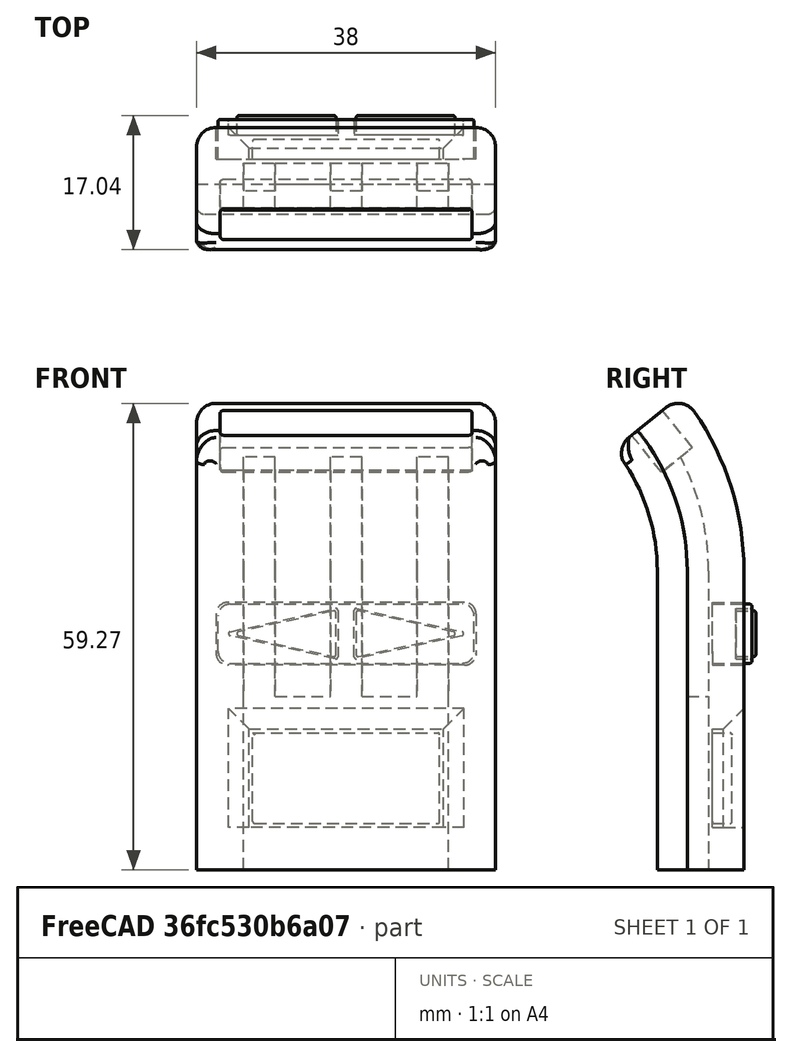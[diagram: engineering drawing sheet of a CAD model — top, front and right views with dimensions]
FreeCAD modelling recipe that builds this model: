
FCSTD DOCUMENT  (FreeCAD 0.20R29603 (Git))
Label: arm
License: All rights reserved
LicenseURL: http://en.wikipedia.org/wiki/All_rights_reserved
objects: Part::Box×22, Part::MultiFuse×15, Part::Cut×13, Part::Fillet×10, Part::Cylinder×9, Sketcher::SketchObject×4, PartDesign::Pad×4, PartDesign::Body×4, Part::MultiCommon×3, Part::Wedge×2, Mesh::Feature×1, Spreadsheet::Sheet×1
note: 90 computed .brp shape members not serialized (recipe doc carries the construction recipe); baked Part::Feature solids carry a one-line shape summary decoded from their .brp

FEATURE [Mesh::Feature] Display_Arm
  Placement = pos=(0,13.65,-35) rot=(0,0,1;0rad)
FEATURE [Part::Cylinder] Cylinder  label="Underside cylinder"
  Angle = 360
  AttacherType = Attacher::AttachEngine3D
  FirstAngle = 0
  Height = 42
  Placement = pos=(-2,-6.5,0) rot=(0,-1,0;4.71239rad)
  Radius = 24.5
  SecondAngle = 0
  expr: .Placement.Base.y = -Spreadsheet.B1 + 18
  expr: Radius = Spreadsheet.B1
FEATURE [Spreadsheet::Sheet] Spreadsheet
  cells = A1=underside radius; B1=24.5; D1=triangle width; E1=5.9; G1=6.5; A2=topside radius; B2=40; D2=triangle height; E2=12.5; F2=1.04; G2=13.75; A3=Arm thickness; B3=11; D3=triangle filet; E3=0.25; G3==E3 * F2; A4=bisect radius; B4=28.3; D4=filet top; E4=0.25; G4==E4 * F2; A5=led channel cut; B5=31
FEATURE [Part::Box] Box  label="Cube"
  AttacherType = Attacher::AttachEngine3D
  Height = 52
  Length = 42
  Placement = pos=(-2,18,0) rot=(1,0,0;3.14159rad)
  Width = 49
  expr: Width = Spreadsheet.B1 * 2
FEATURE [Part::Cylinder] Cylinder001  label="top cylinder"
  Angle = 360
  AttacherType = Attacher::AttachEngine3D
  FirstAngle = 0
  Height = 42
  Placement = pos=(-2,-6.5,0) rot=(0,1,0;1.5708rad)
  Radius = 35.5
  SecondAngle = 0
  expr: .Placement.Base.y = -Spreadsheet.B1 + 18
  expr: Radius = Spreadsheet.B1 + Spreadsheet.B3
FEATURE [Part::Box] Box001  label="Cube001"
  AttacherType = Attacher::AttachEngine3D
  Height = 52
  Length = 42
  Placement = pos=(-2,29,0) rot=(1,0,0;3.14159rad)
  Width = 71
  expr: .Placement.Base.y = 18 + Spreadsheet.B3
  expr: Width = (Spreadsheet.B1 + Spreadsheet.B3) * 2
FEATURE [Part::MultiFuse] Fusion  label="Underside cut"
  Shapes = -> [Cylinder,Box]
FEATURE [Part::MultiFuse] Fusion001  label="Topside intersect"
  Shapes = -> [Cylinder001,Box001]
FEATURE [Part::Box] Box002  label="Cube002"
  AttacherType = Attacher::AttachEngine3D
  Height = 76
  Length = 38
  Placement = pos=(0,10,-38) rot=(0,0,1;0rad)
  Width = 20
FEATURE [Part::Cut] Cut
  Base = -> Box002
  Tool = -> Fusion
FEATURE [Part::MultiCommon] Common
  Shapes = -> [Cut,Fusion001]
FEATURE [Part::Box] Box003  label="Cube003"
  AttacherType = Attacher::AttachEngine3D
  Height = 27
  Length = 56
  Placement = pos=(-5,-6.5,0) rot=(-1,0,0;5.60251rad)
  Width = 48
FEATURE [Part::Cut] Cut001
  Base = -> Common
  Tool = -> Box003
FEATURE [Part::Fillet] Fillet
  Base = -> Cut001
  Edges = 12 edges: [Edge1 r=2.5,Edge2 r=2.5,Edge3 r=2.5,Edge5 r=1,Edge6 r=1,Edge7 r=2.5,Edge8 r=2.5,Edge9 r=2.5,Edge10 r=2.5,Edge12 r=2.5,Edge17 r=1,Edge18 r=1]
FEATURE [Part::Box] Box004  label="Cube004"
  AttacherType = Attacher::AttachEngine3D
  Height = 52
  Length = 42
  Placement = pos=(-2,21.8,0) rot=(1,0,0;3.14159rad)
  Width = 56.6
  expr: .Placement.Base.y = 18 + Spreadsheet.B4 - Spreadsheet.B1
  expr: Width = Spreadsheet.B4 * 2
FEATURE [Part::Cylinder] Cylinder002  label="top cylinder001"
  Angle = 360
  AttacherType = Attacher::AttachEngine3D
  FirstAngle = 0
  Height = 42
  Placement = pos=(-2,-6.5,0) rot=(0,1,0;1.5708rad)
  Radius = 28.3
  SecondAngle = 0
  expr: .Placement.Base.y = -Spreadsheet.B1 + 18
  expr: Radius = Spreadsheet.B4
FEATURE [Part::MultiFuse] Fusion002  label="Bisect intersect"
  Shapes = -> [Box004,Cylinder002]
FEATURE [Sketcher::SketchObject] Sketch
  FullyConstrained = true
  MapMode = 5
  Placement = pos=(0,0,0) rot=(1,0,0;1.5708rad)
  Support = -> [XZ_Plane]
  expr: .Constraints.Base filet = Spreadsheet.E3
  expr: .Constraints.Base filet 2 = Spreadsheet.E3
  expr: .Constraints.base = Spreadsheet.E1
  expr: .Constraints.filet top = Spreadsheet.E4
  expr: Constraints[6] = (Spreadsheet.E1 * Spreadsheet.E1 + Spreadsheet.E2 * Spreadsheet.E2) ^ (1 / 2)
  expr: Constraints[7] = (Spreadsheet.E1 * Spreadsheet.E1 + Spreadsheet.E2 * Spreadsheet.E2) ^ (1 / 2)
  sketch-geometry (10):
    g0: LineSegment StartX=-0.24424 StartY=5.95617 StartZ=0 EndX=-2.88373 EndY=-6.12642 EndZ=0
    g1: LineSegment StartX=-2.63949 StartY=-6.42977 StartZ=0 EndX=2.63949 EndY=-6.42977 EndZ=0
    g2: LineSegment StartX=2.88373 StartY=-6.12642 StartZ=0 EndX=0.24424 EndY=5.95617 EndZ=0
    g3: Circle CenterX=0 CenterY=0 CenterZ=0 NormalX=0 NormalY=0 NormalZ=1 AngleXU=0 Radius=7.07421
    g4: ArcOfCircle CenterX=1.3e-15 CenterY=5.90282 CenterZ=0 NormalX=0 NormalY=0 NormalZ=1 AngleXU=0 Radius=0.25 StartAngle=0.215075 EndAngle=2.92652
    g5: GeomPoint X=1.5e-15 Y=7.07421 Z=0
    g6: ArcOfCircle CenterX=-2.63949 CenterY=-6.17977 CenterZ=0 NormalX=0 NormalY=0 NormalZ=1 AngleXU=0 Radius=0.25 StartAngle=2.92652 EndAngle=4.71239
    g7: GeomPoint X=-2.95 Y=-6.42977 Z=0
    g8: ArcOfCircle CenterX=2.63949 CenterY=-6.17977 CenterZ=0 NormalX=0 NormalY=0 NormalZ=1 AngleXU=0 Radius=0.25 StartAngle=4.71239 EndAngle=6.49826
    g9: GeomPoint X=2.95 Y=-6.42977 Z=0
  constraints (23):
    c: PointOnObject(g7,g3)
    c: PointOnObject(g9,g3)
    c: PointOnObject(g5,g3)
    c: Coincident(g3,g-1)
    c: Horizontal(g1)
    c: Distance(g9,g7) = 5.9  'base'
    c: Distance(g9,g5) = 13.8224
    c: Distance(g7,g5) = 13.8224
    c: PointOnObject(g5,g0)
    c: PointOnObject(g5,g2)
    c: Tangent(g0,g4) = -1.5708
    c: Tangent(g2,g4) = -1.5708
    c: Radius(g4) = 0.25  'filet top'
    c: PointOnObject(g7,g0)
    c: PointOnObject(g7,g1)
    c: Tangent(g0,g6) = -1.5708
    c: Tangent(g1,g6) = -1.5708
    c: PointOnObject(g9,g1)
    c: PointOnObject(g9,g2)
    c: Tangent(g1,g8) = -1.5708
    c: Tangent(g2,g8) = -1.5708
    c: Radius(g8) = 0.25  'Base filet'
    c: Radius(g6) = 0.25  'Base filet 2'
FEATURE [PartDesign::Pad] Pad
  Direction = (0,-1,2e-16)
  Length = 2.5
  Length2 = 10
  Placement = pos=(0,0,0) rot=(1,0,0;1.5708rad)
  Profile = -> Sketch
  ReferenceAxis = -> Sketch [N_Axis]
  Type = 0
FEATURE [PartDesign::Body] Body
  Group = -> [Sketch,Pad]
  Origin = -> Origin
  Placement = pos=(26.7,63,-8) rot=(0,1,0;1.5708rad)
  Tip = -> Pad
FEATURE [Sketcher::SketchObject] Sketch001
  FullyConstrained = true
  MapMode = 5
  Placement = pos=(0,0,0) rot=(1,0,0;1.5708rad)
  Support = -> [XZ_Plane]
  expr: .Constraints.Base filet = Spreadsheet.G3
  expr: .Constraints.Base filet 2 = Spreadsheet.G3
  expr: .Constraints.base = Spreadsheet.G1
  expr: .Constraints.filet top = Spreadsheet.G4
  expr: .Constraints.hyp 1 = (Spreadsheet.G1 ^ 2 + Spreadsheet.G2 ^ 2) ^ (1 / 2)
  expr: .Constraints.hyp 2 = (Spreadsheet.G1 ^ 2 + Spreadsheet.G2 ^ 2) ^ (1 / 2)
  sketch-geometry (10):
    g0: LineSegment StartX=-0.253994 StartY=6.62313 StartZ=0 EndX=-3.18097 EndY=-6.75781 EndZ=0
    g1: LineSegment StartX=-2.92698 StartY=-7.07337 StartZ=0 EndX=2.92698 EndY=-7.07337 EndZ=0
    g2: LineSegment StartX=3.18097 StartY=-6.75781 StartZ=0 EndX=0.253994 EndY=6.62313 EndZ=0
    g3: Circle CenterX=0 CenterY=0 CenterZ=0 NormalX=0 NormalY=0 NormalZ=1 AngleXU=0 Radius=7.78429
    g4: ArcOfCircle CenterX=-1e-15 CenterY=6.56757 CenterZ=0 NormalX=0 NormalY=0 NormalZ=1 AngleXU=0 Radius=0.26 StartAngle=0.21535 EndAngle=2.92624
    g5: GeomPoint X=-1.1e-15 Y=7.78429 Z=0
    g6: ArcOfCircle CenterX=-2.92698 CenterY=-6.81337 CenterZ=0 NormalX=0 NormalY=0 NormalZ=1 AngleXU=0 Radius=0.26 StartAngle=2.92624 EndAngle=4.71239
    g7: GeomPoint X=-3.25 Y=-7.07337 Z=0
    g8: ArcOfCircle CenterX=2.92698 CenterY=-6.81337 CenterZ=0 NormalX=0 NormalY=0 NormalZ=1 AngleXU=0 Radius=0.26 StartAngle=4.71239 EndAngle=6.49854
    g9: GeomPoint X=3.25 Y=-7.07337 Z=0
  constraints (23):
    c: PointOnObject(g7,g3)
    c: PointOnObject(g9,g3)
    c: PointOnObject(g5,g3)
    c: Coincident(g3,g-1)
    c: Horizontal(g1)
    c: Distance(g9,g7) = 6.5  'base'
    c: Distance(g9,g5) = 15.209  'hyp 1'
    c: Distance(g7,g5) = 15.209  'hyp 2'
    c: PointOnObject(g5,g0)
    c: PointOnObject(g5,g2)
    c: Tangent(g0,g4) = -1.5708
    c: Tangent(g2,g4) = -1.5708
    c: Radius(g4) = 0.26  'filet top'
    c: PointOnObject(g7,g0)
    c: PointOnObject(g7,g1)
    c: Tangent(g0,g6) = -1.5708
    c: Tangent(g1,g6) = -1.5708
    c: PointOnObject(g9,g1)
    c: PointOnObject(g9,g2)
    c: Tangent(g1,g8) = -1.5708
    c: Tangent(g2,g8) = -1.5708
    c: Radius(g8) = 0.26  'Base filet'
    c: Radius(g6) = 0.26  'Base filet 2'
FEATURE [PartDesign::Pad] Pad001
  Direction = (0,-1,2e-16)
  Length = 10
  Length2 = 10
  Placement = pos=(0,0,0) rot=(1,0,0;1.5708rad)
  Profile = -> Sketch001
  ReferenceAxis = -> Sketch001 [N_Axis]
  Type = 0
FEATURE [PartDesign::Body] Body001
  Group = -> [Sketch001,Pad001]
  Origin = -> Origin001
  Placement = pos=(27.1,63,-8) rot=(0,1,0;1.5708rad)
  Tip = -> Pad001
FEATURE [Sketcher::SketchObject] Sketch002
  FullyConstrained = true
  MapMode = 5
  Placement = pos=(0,0,0) rot=(1,0,0;1.5708rad)
  Support = -> [XZ_Plane]
  sketch-geometry (10):
    g0: LineSegment StartX=-0.24424 StartY=5.95617 StartZ=0 EndX=-2.88373 EndY=-6.12642 EndZ=0
    g1: LineSegment StartX=-2.63949 StartY=-6.42977 StartZ=0 EndX=2.63949 EndY=-6.42977 EndZ=0
    g2: LineSegment StartX=2.88373 StartY=-6.12642 StartZ=0 EndX=0.24424 EndY=5.95617 EndZ=0
    g3: Circle CenterX=0 CenterY=0 CenterZ=0 NormalX=0 NormalY=0 NormalZ=1 AngleXU=0 Radius=7.07421
    g4: ArcOfCircle CenterX=1.3e-15 CenterY=5.90282 CenterZ=0 NormalX=0 NormalY=0 NormalZ=1 AngleXU=0 Radius=0.25 StartAngle=0.215075 EndAngle=2.92652
    g5: GeomPoint X=1.5e-15 Y=7.07421 Z=0
    g6: ArcOfCircle CenterX=-2.63949 CenterY=-6.17977 CenterZ=0 NormalX=0 NormalY=0 NormalZ=1 AngleXU=0 Radius=0.25 StartAngle=2.92652 EndAngle=4.71239
    g7: GeomPoint X=-2.95 Y=-6.42977 Z=0
    g8: ArcOfCircle CenterX=2.63949 CenterY=-6.17977 CenterZ=0 NormalX=0 NormalY=0 NormalZ=1 AngleXU=0 Radius=0.25 StartAngle=4.71239 EndAngle=6.49826
    g9: GeomPoint X=2.95 Y=-6.42977 Z=0
  constraints (23):
    c: PointOnObject(g7,g3)
    c: PointOnObject(g9,g3)
    c: PointOnObject(g5,g3)
    c: Coincident(g3,g-1)
    c: Horizontal(g1)
    c: Distance(g9,g7) = 5.9  'base'
    c: Distance(g9,g5) = 13.8224
    c: Distance(g7,g5) = 13.8224
    c: PointOnObject(g5,g0)
    c: PointOnObject(g5,g2)
    c: Tangent(g0,g4) = -1.5708
    c: Tangent(g2,g4) = -1.5708
    c: Radius(g4) = 0.25  'filet top'
    c: PointOnObject(g7,g0)
    c: PointOnObject(g7,g1)
    c: Tangent(g0,g6) = -1.5708
    c: Tangent(g1,g6) = -1.5708
    c: PointOnObject(g9,g1)
    c: PointOnObject(g9,g2)
    c: Tangent(g1,g8) = -1.5708
    c: Tangent(g2,g8) = -1.5708
    c: Radius(g8) = 0.25  'Base filet'
    c: Radius(g6) = 0.25  'Base filet 2'
FEATURE [PartDesign::Pad] Pad002
  Direction = (0,-1,2e-16)
  Length = 2.5
  Length2 = 10
  Placement = pos=(0,0,0) rot=(1,0,0;1.5708rad)
  Profile = -> Sketch002
  ReferenceAxis = -> Sketch002 [N_Axis]
  Type = 0
FEATURE [PartDesign::Body] Body002
  Group = -> [Sketch002,Pad002]
  Origin = -> Origin002
  Placement = pos=(11.3,63,-8) rot=(0,-1,0;1.5708rad)
  Tip = -> Pad002
FEATURE [Sketcher::SketchObject] Sketch003
  FullyConstrained = true
  MapMode = 5
  Placement = pos=(0,0,0) rot=(1,0,0;1.5708rad)
  Support = -> [XZ_Plane]
  sketch-geometry (10):
    g0: LineSegment StartX=-0.253994 StartY=6.62313 StartZ=0 EndX=-3.18097 EndY=-6.75781 EndZ=0
    g1: LineSegment StartX=-2.92698 StartY=-7.07337 StartZ=0 EndX=2.92698 EndY=-7.07337 EndZ=0
    g2: LineSegment StartX=3.18097 StartY=-6.75781 StartZ=0 EndX=0.253994 EndY=6.62313 EndZ=0
    g3: Circle CenterX=0 CenterY=0 CenterZ=0 NormalX=0 NormalY=0 NormalZ=1 AngleXU=0 Radius=7.78429
    g4: ArcOfCircle CenterX=-1e-15 CenterY=6.56757 CenterZ=0 NormalX=0 NormalY=0 NormalZ=1 AngleXU=0 Radius=0.26 StartAngle=0.21535 EndAngle=2.92624
    g5: GeomPoint X=-1.1e-15 Y=7.78429 Z=0
    g6: ArcOfCircle CenterX=-2.92698 CenterY=-6.81337 CenterZ=0 NormalX=0 NormalY=0 NormalZ=1 AngleXU=0 Radius=0.26 StartAngle=2.92624 EndAngle=4.71239
    g7: GeomPoint X=-3.25 Y=-7.07337 Z=0
    g8: ArcOfCircle CenterX=2.92698 CenterY=-6.81337 CenterZ=0 NormalX=0 NormalY=0 NormalZ=1 AngleXU=0 Radius=0.26 StartAngle=4.71239 EndAngle=6.49854
    g9: GeomPoint X=3.25 Y=-7.07337 Z=0
  constraints (23):
    c: PointOnObject(g7,g3)
    c: PointOnObject(g9,g3)
    c: PointOnObject(g5,g3)
    c: Coincident(g3,g-1)
    c: Horizontal(g1)
    c: Distance(g9,g7) = 6.5  'base'
    c: Distance(g9,g5) = 15.209  'hyp 1'
    c: Distance(g7,g5) = 15.209  'hyp 2'
    c: PointOnObject(g5,g0)
    c: PointOnObject(g5,g2)
    c: Tangent(g0,g4) = -1.5708
    c: Tangent(g2,g4) = -1.5708
    c: Radius(g4) = 0.26  'filet top'
    c: PointOnObject(g7,g0)
    c: PointOnObject(g7,g1)
    c: Tangent(g0,g6) = -1.5708
    c: Tangent(g1,g6) = -1.5708
    c: PointOnObject(g9,g1)
    c: PointOnObject(g9,g2)
    c: Tangent(g1,g8) = -1.5708
    c: Tangent(g2,g8) = -1.5708
    c: Radius(g8) = 0.26  'Base filet'
    c: Radius(g6) = 0.26  'Base filet 2'
FEATURE [PartDesign::Pad] Pad003
  Direction = (0,-1,2e-16)
  Length = 10
  Length2 = 10
  Placement = pos=(0,0,0) rot=(1,0,0;1.5708rad)
  Profile = -> Sketch003
  ReferenceAxis = -> Sketch003 [N_Axis]
  Type = 0
FEATURE [PartDesign::Body] Body003
  Group = -> [Sketch003,Pad003]
  Origin = -> Origin003
  Placement = pos=(10.9,63,-8) rot=(0,1,0;4.71239rad)
  Tip = -> Pad003
FEATURE [Part::Box] Box005  label="Cube005"
  AttacherType = Attacher::AttachEngine3D
  Height = 7.5
  Length = 32.52
  Placement = pos=(2.75,25,-11.75) rot=(0,0,1;0rad)
  Width = 5
FEATURE [Part::Box] Box006  label="Cube006"
  AttacherType = Attacher::AttachEngine3D
  Height = 8
  Length = 33.02
  Placement = pos=(2.5,25,-12) rot=(0,0,1;0rad)
  Width = 5
FEATURE [Part::Fillet] Fillet001
  Base = -> Box006
  Edges = 4 edges r=1.5: [Edge2,Edge4,Edge6,Edge8]
FEATURE [Part::Cut] Cut002
  Base = -> Fillet
  Tool = -> Fillet001
FEATURE [Part::Fillet] Fillet002
  Base = -> Box005
  Edges = 4 edges r=1.5: [Edge2,Edge4,Edge6,Edge8]
FEATURE [Part::MultiFuse] Fusion003  label="wedge holes"
  Placement = pos=(0,-25,0) rot=(0,0,1;0rad)
  Shapes = -> [Body003,Body001]
FEATURE [Part::Cut] Cut003  label="panel"
  Base = -> Fillet002
  Tool = -> Fusion003
FEATURE [Part::MultiFuse] Fusion004  label="Arrows"
  Placement = pos=(0,-32.5,0) rot=(0,0,1;0rad)
  Shapes = -> [Body002,Body]
FEATURE [Part::Wedge] Wedge
  AttacherType = Attacher::AttachEngine3D
  Placement = pos=(6.65,26.4,-24.1) rot=(0,0,1;0rad)
  X2max = 30.75
  X2min = -6
  Xmax = 24.75
  Xmin = 0
  Ymax = 6
  Ymin = 0
  Z2max = 10
  Z2min = -8.5
  Zmax = 4
  Zmin = -8.5
FEATURE [Part::Box] Box007  label="Cube007"
  AttacherType = Attacher::AttachEngine3D
  Height = 12.5
  Length = 24.75
  Placement = pos=(6.65,25,-32.6) rot=(0,0,1;0rad)
  Width = 5
FEATURE [Part::Box] Box008  label="Cube008"
  AttacherType = Attacher::AttachEngine3D
  Height = 11.5
  Length = 23.75
  Placement = pos=(7.15,25,-32.1) rot=(0,0,1;0rad)
  Width = 2.5
FEATURE [Part::MultiFuse] Fusion005
  Shapes = -> [Box007,Wedge]
FEATURE [Part::Cut] Cut004
  Base = -> Cut002
  Tool = -> Fusion005
FEATURE [Part::Fillet] Fillet003  label="arrowhole"
  Base = -> Cut003
  Edges = 20 edges r=0.25: [Edge3,Edge13,Edge14,Edge15,Edge16,Edge17,Edge18,Edge19,Edge20,Edge21,Edge22,Edge23,Edge24,Edge25,Edge26,Edge27,Edge28,Edge29,Edge30,Edge31]
FEATURE [Part::Fillet] Fillet004  label="arrows"
  Base = -> Fusion004
  Edges = 12 edges r=0.25: [Edge3,Edge6,Edge9,Edge12,Edge15,Edge17,Edge21,Edge24,Edge27,Edge30,Edge33,Edge35]
FEATURE [Part::Fillet] Fillet005  label="button"
  Base = -> Box008
  Edges = 7 edges r=0.25: [Edge3,Edge4,Edge6,Edge7,Edge8,Edge11,Edge12]
FEATURE [Part::Box] Box009  label="Cube009"
  AttacherType = Attacher::AttachEngine3D
  Height = 27
  Length = 32
  Placement = pos=(3.02,18.5342,12.5131) rot=(1,0,0;0.680678rad)
  Width = 5.02
FEATURE [Part::Fillet] Fillet006
  Base = -> Box009
  Edges = 4 edges r=0.5: [Edge1,Edge3,Edge5,Edge7]
FEATURE [Part::Cut] Cut005
  Base = -> Cut004
  Tool = -> Fillet006
FEATURE [Part::Box] Box010  label="Cube010"
  AttacherType = Attacher::AttachEngine3D
  Height = 52
  Length = 42
  Placement = pos=(-2,18,0) rot=(1,0,0;3.14159rad)
  Width = 49
  expr: Width = Spreadsheet.B1 * 2
FEATURE [Part::Box] Box011  label="Cube011"
  AttacherType = Attacher::AttachEngine3D
  Height = 52
  Length = 42
  Placement = pos=(-2,29,0) rot=(1,0,0;3.14159rad)
  Width = 71
  expr: .Placement.Base.y = 18 + Spreadsheet.B3
  expr: Width = (Spreadsheet.B1 + Spreadsheet.B3) * 2
FEATURE [Part::Box] Box012  label="Cube012"
  AttacherType = Attacher::AttachEngine3D
  Height = 76
  Length = 38
  Placement = pos=(0,10,-38) rot=(0,0,1;0rad)
  Width = 20
FEATURE [Part::Box] Box013  label="Cube013"
  AttacherType = Attacher::AttachEngine3D
  Height = 27
  Length = 56
  Placement = pos=(-5,-6.5,0) rot=(1,0,0;0.680678rad)
  Width = 48
FEATURE [Part::Box] Box014  label="Cube014"
  AttacherType = Attacher::AttachEngine3D
  Height = 8
  Length = 33.02
  Placement = pos=(2.5,25,-12) rot=(0,0,1;0rad)
  Width = 5
FEATURE [Part::Box] Box015  label="Cube015"
  AttacherType = Attacher::AttachEngine3D
  Height = 12.5
  Length = 24.75
  Placement = pos=(6.65,25,-32.6) rot=(0,0,1;0rad)
  Width = 5
FEATURE [Part::Box] Box016  label="Cube016"
  AttacherType = Attacher::AttachEngine3D
  Height = 27
  Length = 32
  Placement = pos=(3.02,18.5342,12.5131) rot=(1,0,0;0.680678rad)
  Width = 5.02
FEATURE [Part::Cylinder] Cylinder003  label="Underside cylinder001"
  Angle = 360
  AttacherType = Attacher::AttachEngine3D
  FirstAngle = 0
  Height = 42
  Placement = pos=(-2,-6.5,0) rot=(0,1,0;1.5708rad)
  Radius = 24.5
  SecondAngle = 0
  expr: .Placement.Base.y = -Spreadsheet.B1 + 18
  expr: Radius = Spreadsheet.B1
FEATURE [Part::Cylinder] Cylinder004  label="top cylinder002"
  Angle = 360
  AttacherType = Attacher::AttachEngine3D
  FirstAngle = 0
  Height = 42
  Placement = pos=(-2,-6.5,0) rot=(0,1,0;1.5708rad)
  Radius = 35.5
  SecondAngle = 0
  expr: .Placement.Base.y = -Spreadsheet.B1 + 18
  expr: Radius = Spreadsheet.B1 + Spreadsheet.B3
FEATURE [Part::Fillet] Fillet008
  Base = -> Box014
  Edges = 4 edges r=1.5: [Edge2,Edge4,Edge6,Edge8]
FEATURE [Part::Fillet] Fillet009
  Base = -> Box016
  Edges = 4 edges r=0.5: [Edge1,Edge3,Edge5,Edge7]
FEATURE [Part::MultiFuse] Fusion006  label="Underside cut001"
  Shapes = -> [Cylinder003,Box010]
FEATURE [Part::Cut] Cut006
  Base = -> Box012
  Tool = -> Fusion006
FEATURE [Part::MultiFuse] Fusion007  label="Topside intersect001"
  Shapes = -> [Cylinder004,Box011]
FEATURE [Part::MultiCommon] Common001
  Shapes = -> [Cut006,Fusion007]
FEATURE [Part::Cut] Cut007
  Base = -> Common001
  Tool = -> Box013
FEATURE [Part::Fillet] Fillet007
  Base = -> Cut007
  Edges = 12 edges: [Edge1 r=2.5,Edge2 r=2.5,Edge3 r=2.5,Edge5 r=1,Edge6 r=1,Edge7 r=2.5,Edge8 r=2.5,Edge9 r=2.5,Edge10 r=2.5,Edge12 r=2.5,Edge17 r=1,Edge18 r=1]
FEATURE [Part::Cut] Cut008
  Base = -> Fillet007
  Tool = -> Fillet008
FEATURE [Part::Wedge] Wedge001
  AttacherType = Attacher::AttachEngine3D
  Placement = pos=(6.65,26.4,-24.1) rot=(0,0,1;0rad)
  X2max = 30.75
  X2min = -6
  Xmax = 24.75
  Xmin = 0
  Ymax = 6
  Ymin = 0
  Z2max = 10
  Z2min = -8.5
  Zmax = 4
  Zmin = -8.5
FEATURE [Part::MultiFuse] Fusion008
  Shapes = -> [Box015,Wedge001]
FEATURE [Part::Cut] Cut009
  Base = -> Cut008
  Tool = -> Fusion008
FEATURE [Part::Cut] Cut010
  Base = -> Cut009
  Tool = -> Fillet009
FEATURE [Part::Box] Box017  label="Cube017"
  AttacherType = Attacher::AttachEngine3D
  Height = 52
  Length = 42
  Placement = pos=(-2,21.8,0) rot=(1,0,0;3.14159rad)
  Width = 56.6
  expr: .Placement.Base.y = 18 + Spreadsheet.B4 - Spreadsheet.B1
  expr: Width = Spreadsheet.B4 * 2
FEATURE [Part::Cylinder] Cylinder005  label="top cylinder003"
  Angle = 360
  AttacherType = Attacher::AttachEngine3D
  FirstAngle = 0
  Height = 42
  Placement = pos=(-2,-6.5,0) rot=(0,1,0;1.5708rad)
  Radius = 28.3
  SecondAngle = 0
  expr: .Placement.Base.y = -Spreadsheet.B1 + 18
  expr: Radius = Spreadsheet.B4
FEATURE [Part::MultiFuse] Fusion009  label="Bisect intersect001"
  Shapes = -> [Box017,Cylinder005]
FEATURE [Part::Cut] Cut011
  Base = -> Cut010
  Tool = -> Fusion009
FEATURE [Part::MultiCommon] Common002  label="bottom"
  Shapes = -> [Cut005,Fusion002]
FEATURE [Part::Box] Box018  label="Cube018"
  AttacherType = Attacher::AttachEngine3D
  Height = 52
  Length = 4
  Placement = pos=(-2,24.5,0) rot=(1,0,0;3.14159rad)
  Width = 62
  expr: .Placement.Base.y = 18 + Spreadsheet.B5 - Spreadsheet.B1
  expr: Width = Spreadsheet.B5 * 2
FEATURE [Part::Cylinder] Cylinder006  label="top cylinder004"
  Angle = 360
  AttacherType = Attacher::AttachEngine3D
  FirstAngle = 0
  Height = 4
  Placement = pos=(-2,-6.5,0) rot=(0,1,0;1.5708rad)
  Radius = 31
  SecondAngle = 0
  expr: .Placement.Base.y = -Spreadsheet.B1 + 18
  expr: Radius = Spreadsheet.B5
FEATURE [Part::MultiFuse] Fusion010  label="led channel"
  Placement = pos=(8,0,0) rot=(0,0,1;0rad)
  Shapes = -> [Box018,Cylinder006]
FEATURE [Part::Box] Box019  label="Cube019"
  AttacherType = Attacher::AttachEngine3D
  Height = 52
  Length = 4
  Placement = pos=(-2,24.5,0) rot=(1,0,0;3.14159rad)
  Width = 62
  expr: .Placement.Base.y = 18 + Spreadsheet.B5 - Spreadsheet.B1
  expr: Width = Spreadsheet.B5 * 2
FEATURE [Part::Cylinder] Cylinder007  label="top cylinder005"
  Angle = 360
  AttacherType = Attacher::AttachEngine3D
  FirstAngle = 0
  Height = 4
  Placement = pos=(-2,-6.5,0) rot=(0,1,0;1.5708rad)
  Radius = 31
  SecondAngle = 0
  expr: .Placement.Base.y = -Spreadsheet.B1 + 18
  expr: Radius = Spreadsheet.B5
FEATURE [Part::MultiFuse] Fusion011  label="led channel001"
  Placement = pos=(19,0,0) rot=(0,0,1;0rad)
  Shapes = -> [Box019,Cylinder007]
FEATURE [Part::Box] Box020  label="Cube020"
  AttacherType = Attacher::AttachEngine3D
  Height = 52
  Length = 4
  Placement = pos=(-2,24.5,0) rot=(1,0,0;3.14159rad)
  Width = 62
  expr: .Placement.Base.y = 18 + Spreadsheet.B5 - Spreadsheet.B1
  expr: Width = Spreadsheet.B5 * 2
FEATURE [Part::Cylinder] Cylinder008  label="top cylinder006"
  Angle = 360
  AttacherType = Attacher::AttachEngine3D
  FirstAngle = 0
  Height = 4
  Placement = pos=(-2,-6.5,0) rot=(0,1,0;1.5708rad)
  Radius = 31
  SecondAngle = 0
  expr: .Placement.Base.y = -Spreadsheet.B1 + 18
  expr: Radius = Spreadsheet.B5
FEATURE [Part::MultiFuse] Fusion012  label="led channel002"
  Placement = pos=(30,0,0) rot=(0,0,1;0rad)
  Shapes = -> [Box020,Cylinder008]
FEATURE [Part::MultiFuse] Fusion013  label="LED channels"
  Shapes = -> [Fusion012,Fusion010,Fusion011]
FEATURE [Part::Box] Box021  label="Cube021"
  AttacherType = Attacher::AttachEngine3D
  Height = 52
  Length = 26
  Placement = pos=(6,24.5,-16) rot=(1,0,0;3.14159rad)
  Width = 62
  expr: .Placement.Base.y = 18 + Spreadsheet.B5 - Spreadsheet.B1
  expr: Width = Spreadsheet.B5 * 2
FEATURE [Part::MultiFuse] Fusion014  label="Electrical channel"
  Shapes = -> [Fusion013,Box021]
FEATURE [Part::Cut] Cut012  label="Top"
  Base = -> Cut011
  Tool = -> Fusion014
